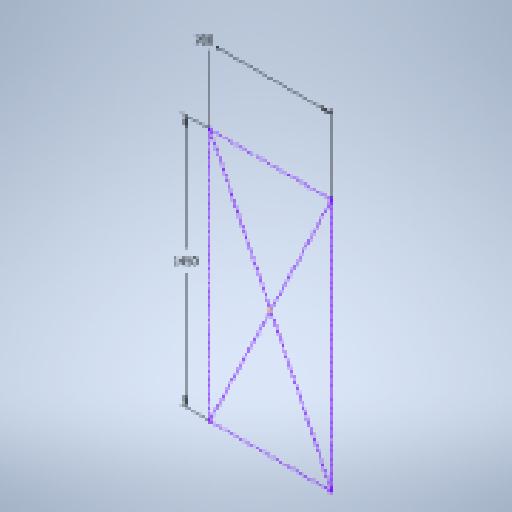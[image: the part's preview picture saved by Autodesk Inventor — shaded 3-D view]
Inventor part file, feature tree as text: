
AUTODESK INVENTOR PART (.ipt)
format: ipt  version: 2023.2 (Build 272271030, 271C)  size: 129,536 bytes
history: native  units: mm
features: sketch x2
ambient origin geometry x8: Origin, YZ Plane, XZ Plane, XY Plane, X Axis, Y Axis, Z Axis, Center Point
feature tree (2):
  sketch  "Sketch2"  dims[d3=1450.0mm d4=700.0mm]
  sketch  "3D Sketch2"
